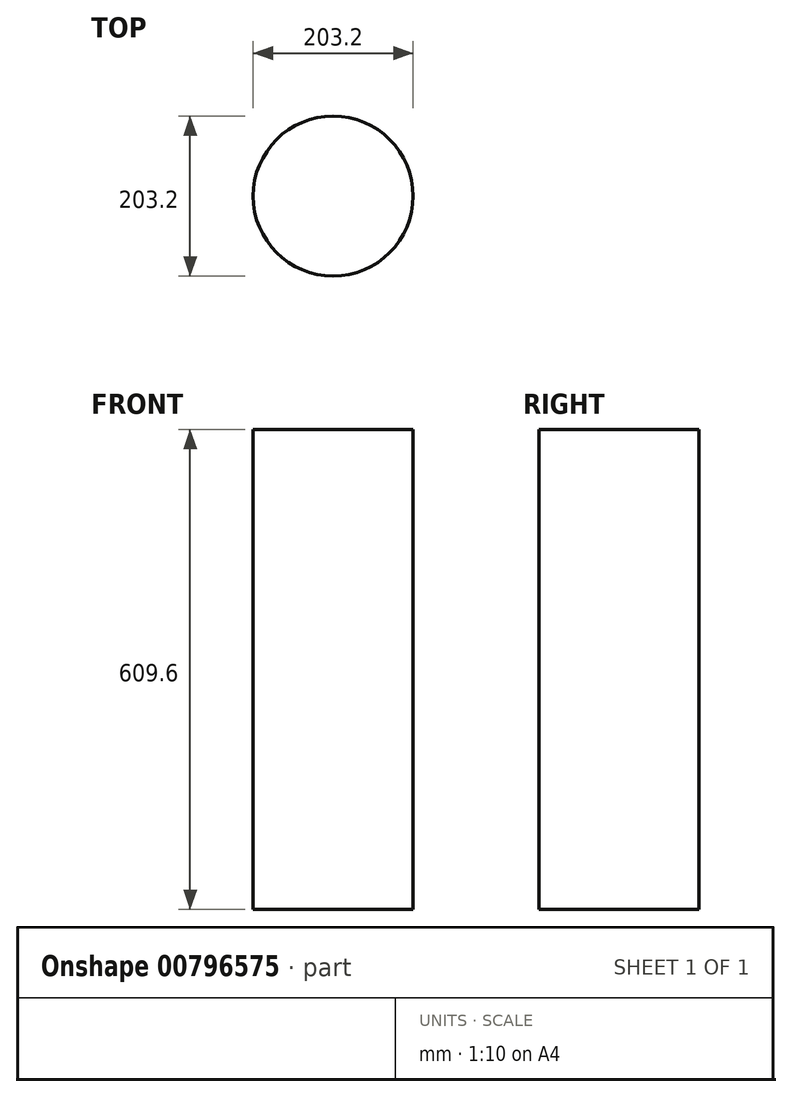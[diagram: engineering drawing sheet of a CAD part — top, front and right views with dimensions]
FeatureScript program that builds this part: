
annotation { "Feature Type Name" : "Feature", "Feature Type Description" : "" }
export const myFeature = defineFeature(function(context is Context, id is Id, definition is map)
    precondition{}
    {
        {
            var Q0;
            Q0=qCreatedBy(makeId("Top.planeOp"),FACE);
            var sketch = newSketch(context, id + "F0", { "sketchPlane" : qUnion([Q0])});
            skCircle(sketch, "E0", {"center": v(-1.1, 0) * mm, "radius": 101.6 * mm});
            skPoint(sketch, "E0.first.point", {"position": v(-71.93, 72.84) * mm});
            skPoint(sketch, "E0.second.point", {"position": v(64.34, -77.72) * mm});
            skPoint(sketch, "E0.third.point", {"position": v(-44.17, -92.02) * mm});
            skSolve(sketch);
        }
        {
            var Q0;
            Q0=makeQuery(id+"F0.imprint","IMPRINT",FACE,{"disambiguationData":[TD([[makeQuery(id+"F0.imprint","IMPRINT",EDGE,{"derivedFrom":sQuery(id+"F0.wireOp",EDGE,"E0")}),1.0]])]});
            extrude(context, id + "F1", {"entities" : qUnion([Q0]), "endBound" : BoundingType.SYMMETRIC, "depth" : 609.6 * mm, "offsetDistance" : 25.4 * mm});
        }
    });
